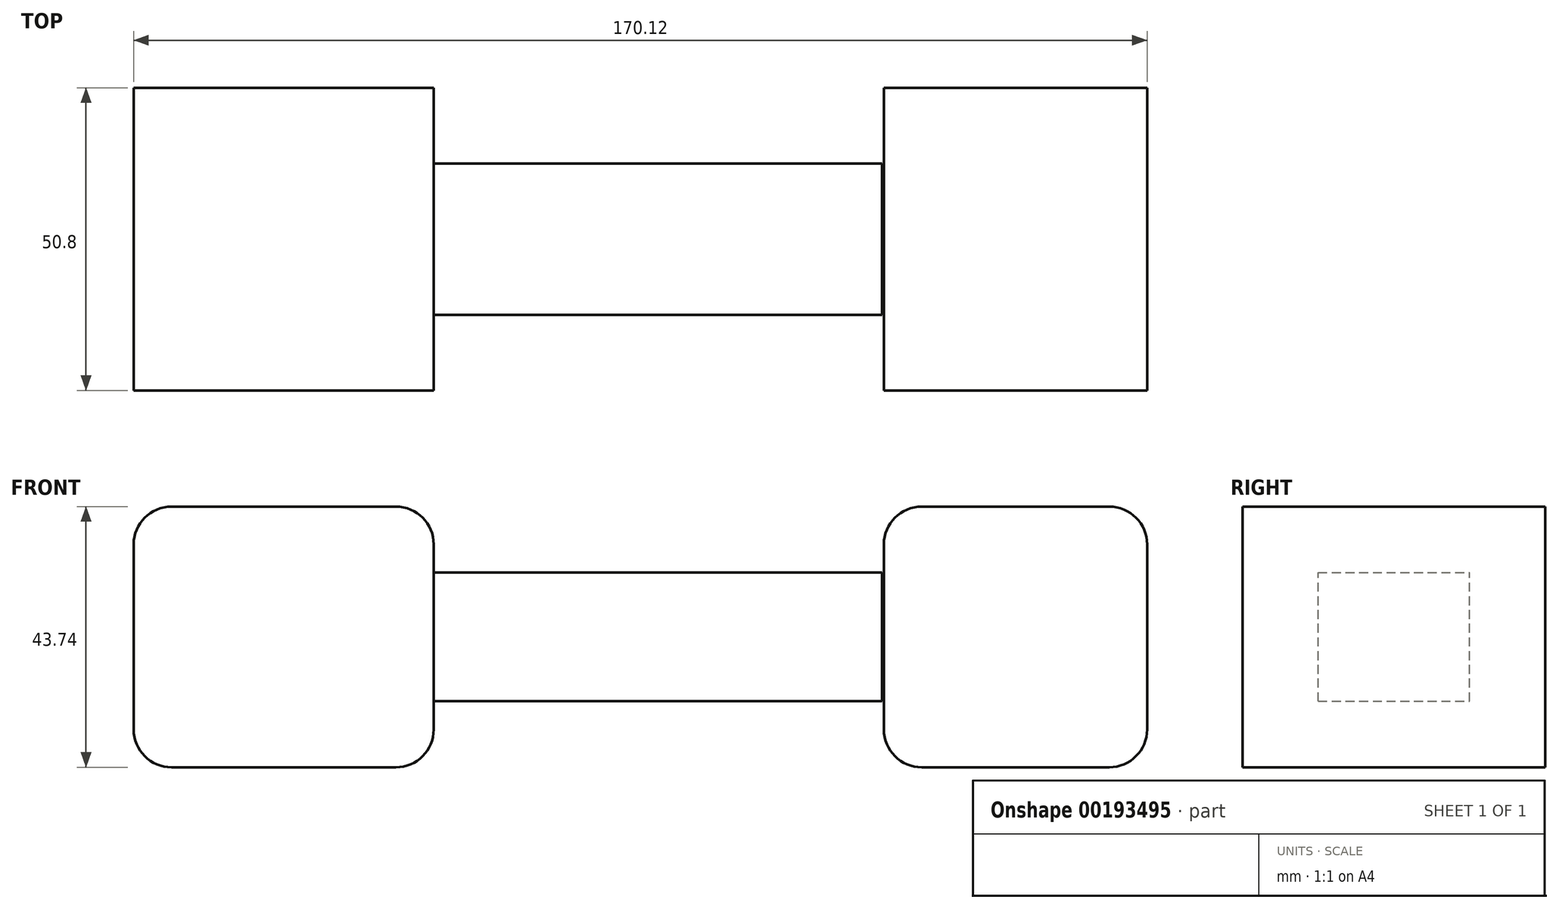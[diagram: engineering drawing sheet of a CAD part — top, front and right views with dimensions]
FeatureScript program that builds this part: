
annotation { "Feature Type Name" : "Feature", "Feature Type Description" : "" }
export const myFeature = defineFeature(function(context is Context, id is Id, definition is map)
    precondition{}
    {
        {
            var Q0;
            Q0=qCreatedBy(makeId("Front.planeOp"),FACE);
            var sketch = newSketch(context, id + "F0", { "sketchPlane" : qUnion([Q0])});
            skLineSegment(sketch, "E0.bottom", {"start": v(-38.1, 10.8) * mm, "end": v(38.1, 10.8) * mm});
            skLineSegment(sketch, "E0.top", {"start": v(-38.1, -10.8) * mm, "end": v(38.1, -10.8) * mm});
            skLineSegment(sketch, "E0.left", {"start": v(-38.1, 10.8) * mm, "end": v(-38.1, -10.8) * mm});
            skLineSegment(sketch, "E0.right", {"start": v(38.1, 10.8) * mm, "end": v(38.1, -10.8) * mm});
            skPoint(sketch, "E0.middle", {"position": v(0, 0) * mm});
            skLineSegment(sketch, "E1.bottom", {"start": v(-81.14, -21.87) * mm, "end": v(-43.47, -21.87) * mm});
            skLineSegment(sketch, "E1.top", {"start": v(-81.14, 21.87) * mm, "end": v(-43.47, 21.87) * mm});
            skLineSegment(sketch, "E1.left", {"start": v(-87.49, -15.52) * mm, "end": v(-87.49, 15.52) * mm});
            skLineSegment(sketch, "E1.right", {"start": v(-37.12, -15.52) * mm, "end": v(-37.12, 15.52) * mm});
            skPoint(sketch, "E1.middle", {"position": v(-62.3, 0) * mm});
            skLineSegment(sketch, "E2.bottom", {"start": v(76.28, -21.87) * mm, "end": v(44.8, -21.87) * mm});
            skLineSegment(sketch, "E2.top", {"start": v(76.28, 21.87) * mm, "end": v(44.8, 21.87) * mm});
            skLineSegment(sketch, "E2.left", {"start": v(82.63, -15.52) * mm, "end": v(82.63, 15.52) * mm});
            skLineSegment(sketch, "E2.right", {"start": v(38.44, -15.52) * mm, "end": v(38.44, 15.52) * mm});
            skPoint(sketch, "E2.middle", {"position": v(60.53, 0) * mm});
            skPoint(sketch, "E2.cornerSnap0", {"position": v(-62.3, -21.87) * mm});
            skPoint(sketch, "E3.visualSharp", {"position": v(-87.49, 21.87) * mm});
            skArc(sketch, "E3.filletArc", {"start": v(-81.14, 21.87) * mm, "mid": v(-85.63, 20.01) * mm, "end": v(-87.49, 15.52) * mm});
            skPoint(sketch, "E4.visualSharp", {"position": v(-37.12, 21.87) * mm});
            skArc(sketch, "E4.filletArc", {"start": v(-37.12, 15.52) * mm, "mid": v(-38.98, 20.01) * mm, "end": v(-43.47, 21.87) * mm});
            skPoint(sketch, "E5.visualSharp", {"position": v(-87.49, -21.87) * mm});
            skArc(sketch, "E5.filletArc", {"start": v(-87.49, -15.52) * mm, "mid": v(-85.63, -20.01) * mm, "end": v(-81.14, -21.87) * mm});
            skPoint(sketch, "E6.visualSharp", {"position": v(-37.12, -21.87) * mm});
            skArc(sketch, "E6.filletArc", {"start": v(-43.47, -21.87) * mm, "mid": v(-38.98, -20.01) * mm, "end": v(-37.12, -15.52) * mm});
            skPoint(sketch, "E7.visualSharp", {"position": v(38.44, 21.87) * mm});
            skArc(sketch, "E7.filletArc", {"start": v(44.8, 21.87) * mm, "mid": v(40.3, 20.01) * mm, "end": v(38.44, 15.52) * mm});
            skPoint(sketch, "E8.visualSharp", {"position": v(82.63, 21.87) * mm});
            skArc(sketch, "E8.filletArc", {"start": v(82.63, 15.52) * mm, "mid": v(80.77, 20.01) * mm, "end": v(76.28, 21.87) * mm});
            skPoint(sketch, "E9.visualSharp", {"position": v(82.63, -21.87) * mm});
            skArc(sketch, "E9.filletArc", {"start": v(76.28, -21.87) * mm, "mid": v(80.77, -20.01) * mm, "end": v(82.63, -15.52) * mm});
            skPoint(sketch, "E10.visualSharp", {"position": v(38.44, -21.87) * mm});
            skArc(sketch, "E10.filletArc", {"start": v(38.44, -15.52) * mm, "mid": v(40.3, -20.01) * mm, "end": v(44.8, -21.87) * mm});
            skSolve(sketch);
        }
        {
            var Q0;
            Q0=makeQuery(id+"F0.imprint","IMPRINT",FACE,{"disambiguationData":[TD([[makeQuery(id+"F0.imprint","IMPRINT",EDGE,{"derivedFrom":sQuery(id+"F0.wireOp",EDGE,"E2.bottom")}),-1.0]])]});
            var Q1;
            {var subQ7=sQuery(id+"F0.wireOp",EDGE,"E0.left");Q1=makeQuery(id+"F0.imprint","IMPRINT",FACE,{"disambiguationData":[TD([[makeQuery(id+"F0.imprint","IMPRINT",EDGE,{"derivedFrom":subQ7}),-1.0]])]});}
            var Q2;
            {var subQ0=sQuery(id+"F0.wireOp",EDGE,"E0.left");Q2=makeQuery(id+"F0.imprint","IMPRINT",FACE,{"disambiguationData":[TD([[makeQuery(id+"F0.imprint","IMPRINT",EDGE,{"derivedFrom":subQ0}),1.0]])]});}
            extrude(context, id + "F1", {"entities" : qUnion([Q0, Q1, Q2]), "endBound" : BoundingType.SYMMETRIC, "depth" : 50.8 * mm});
        }
        {
            var Q0;
            {var subQ0=sQuery(id+"F0.wireOp",EDGE,"E0.right");Q0=makeQuery(id+"F0.imprint","IMPRINT",FACE,{"disambiguationData":[TD([[makeQuery(id+"F0.imprint","IMPRINT",EDGE,{"derivedFrom":subQ0}),-1.0]])]});}
            extrude(context, id + "F2", {"entities" : qUnion([Q0]), "operationType" : NewBodyOperationType.ADD, "endBound" : BoundingType.SYMMETRIC, "depth" : 25.4 * mm});
        }
    });
